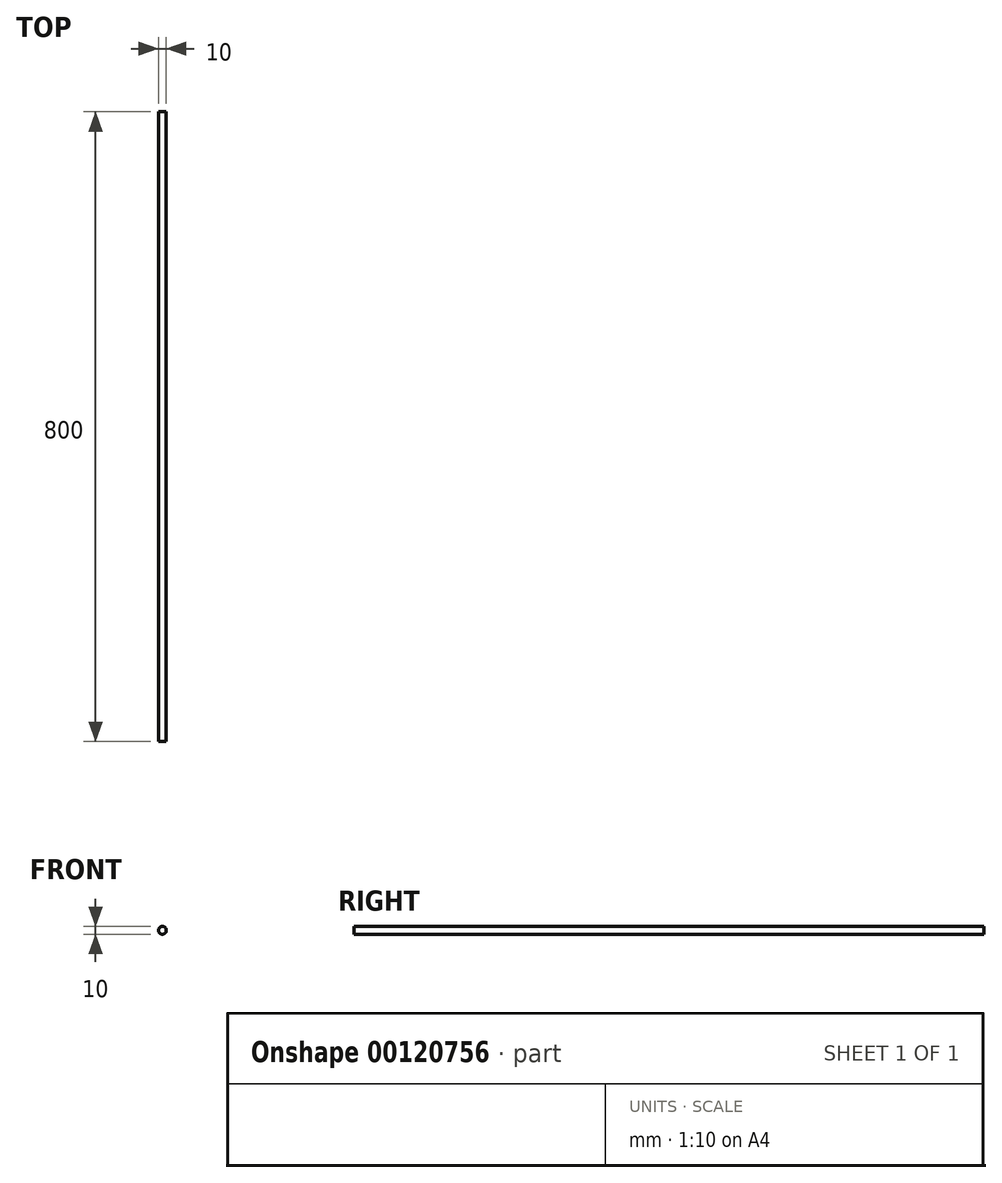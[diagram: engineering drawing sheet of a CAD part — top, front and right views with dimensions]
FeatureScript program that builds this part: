
annotation { "Feature Type Name" : "Feature", "Feature Type Description" : "" }
export const myFeature = defineFeature(function(context is Context, id is Id, definition is map)
    precondition{}
    {
        {
            var Q0;
            Q0=qCreatedBy(makeId("Front.planeOp"),FACE);
            var sketch = newSketch(context, id + "F0", { "sketchPlane" : qUnion([Q0])});
            skCircle(sketch, "E0", {"center": v(0, 0) * mm, "radius": 5 * mm});
            skSolve(sketch);
        }
        {
            var Q0;
            Q0=makeQuery(id+"F0.imprint","IMPRINT",FACE,{"disambiguationData":[TD([[makeQuery(id+"F0.imprint","IMPRINT",EDGE,{"derivedFrom":sQuery(id+"F0.wireOp",EDGE,"E0")}),1.0]])]});
            extrude(context, id + "F1", {"entities" : qUnion([Q0]), "oppositeDirection" : true, "depth" : 800 * mm});
        }
    });
